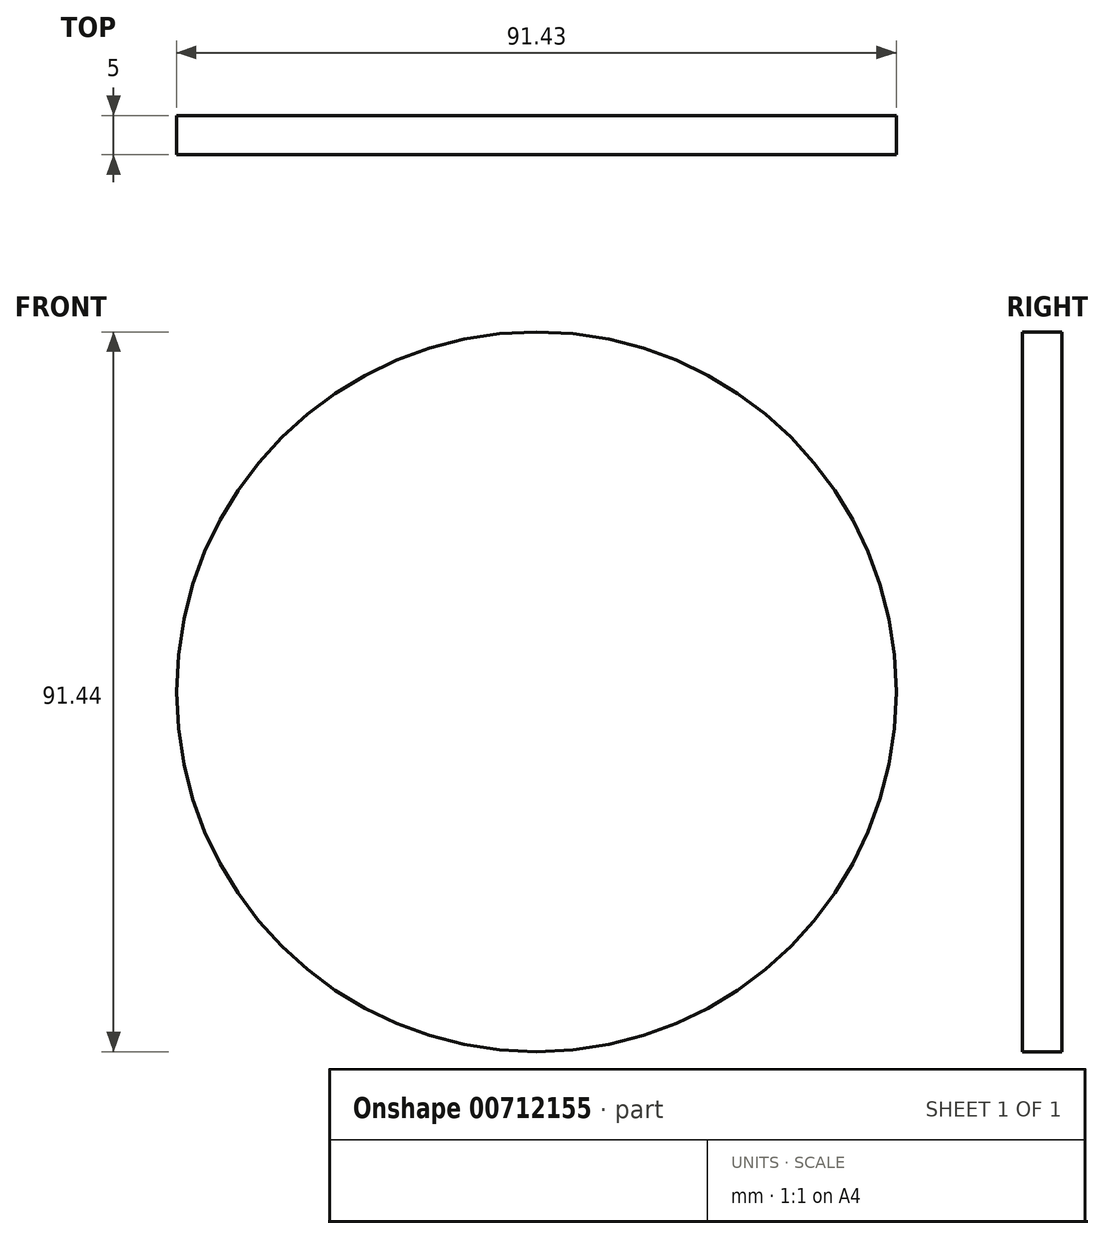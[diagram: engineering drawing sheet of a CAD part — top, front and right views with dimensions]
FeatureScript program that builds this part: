
annotation { "Feature Type Name" : "Feature", "Feature Type Description" : "" }
export const myFeature = defineFeature(function(context is Context, id is Id, definition is map)
    precondition{}
    {
        {
            var Q0;
            Q0=qCreatedBy(makeId("Front.planeOp"),FACE);
            var sketch = newSketch(context, id + "F0", { "sketchPlane" : qUnion([Q0])});
            skCircle(sketch, "E0", {"center": v(-222.72, -41.68) * mm, "radius": 45.72 * mm});
            skSolve(sketch);
        }
        {
            var Q0;
            Q0 = qSketchRegion(id + "F3hvus4aYxQaEos_0", true);
            var Q1;
            Q1=makeQuery(id+"F0.imprint","IMPRINT",FACE,{"disambiguationData":[TD([[makeQuery(id+"F0.imprint","IMPRINT",EDGE,{"derivedFrom":sQuery(id+"F0.wireOp",EDGE,"E0")}),1.0]])]});
            extrude(context, id + "F1", {"entities" : qUnion([Q0, Q1]), "depth" : 5 * mm, "offsetDistance" : 25 * mm});
        }
        {
            var Q0;
            Q0=makeQuery(id+"F1.opExtrude","CAP_FACE",FACE,{"disambiguationData":[OSD([sQuery(id+"F0.wireOp",EDGE,"E0")])],"isStart":false});
            var sketch = newSketch(context, id + "F2", { "sketchPlane" : qUnion([Q0])});
            skCircle(sketch, "E1", {"center": v(-222.72, -41.68) * mm, "radius": 1.52 * mm});
            skSolve(sketch);
        }
        {
            var Q0;
            Q0=makeQuery(id+"F2.imprint","IMPRINT",FACE,{"disambiguationData":[TD([[makeQuery(id+"F2.imprint","IMPRINT",EDGE,{"derivedFrom":sQuery(id+"F2.wireOp",EDGE,"E1")}),1.0]])]});
            extrude(context, id + "F3", {"entities" : qUnion([Q0]), "operationType" : NewBodyOperationType.ADD, "oppositeDirection" : true, "depth" : 0.3 * mm, "offsetDistance" : 25 * mm});
        }
    });
